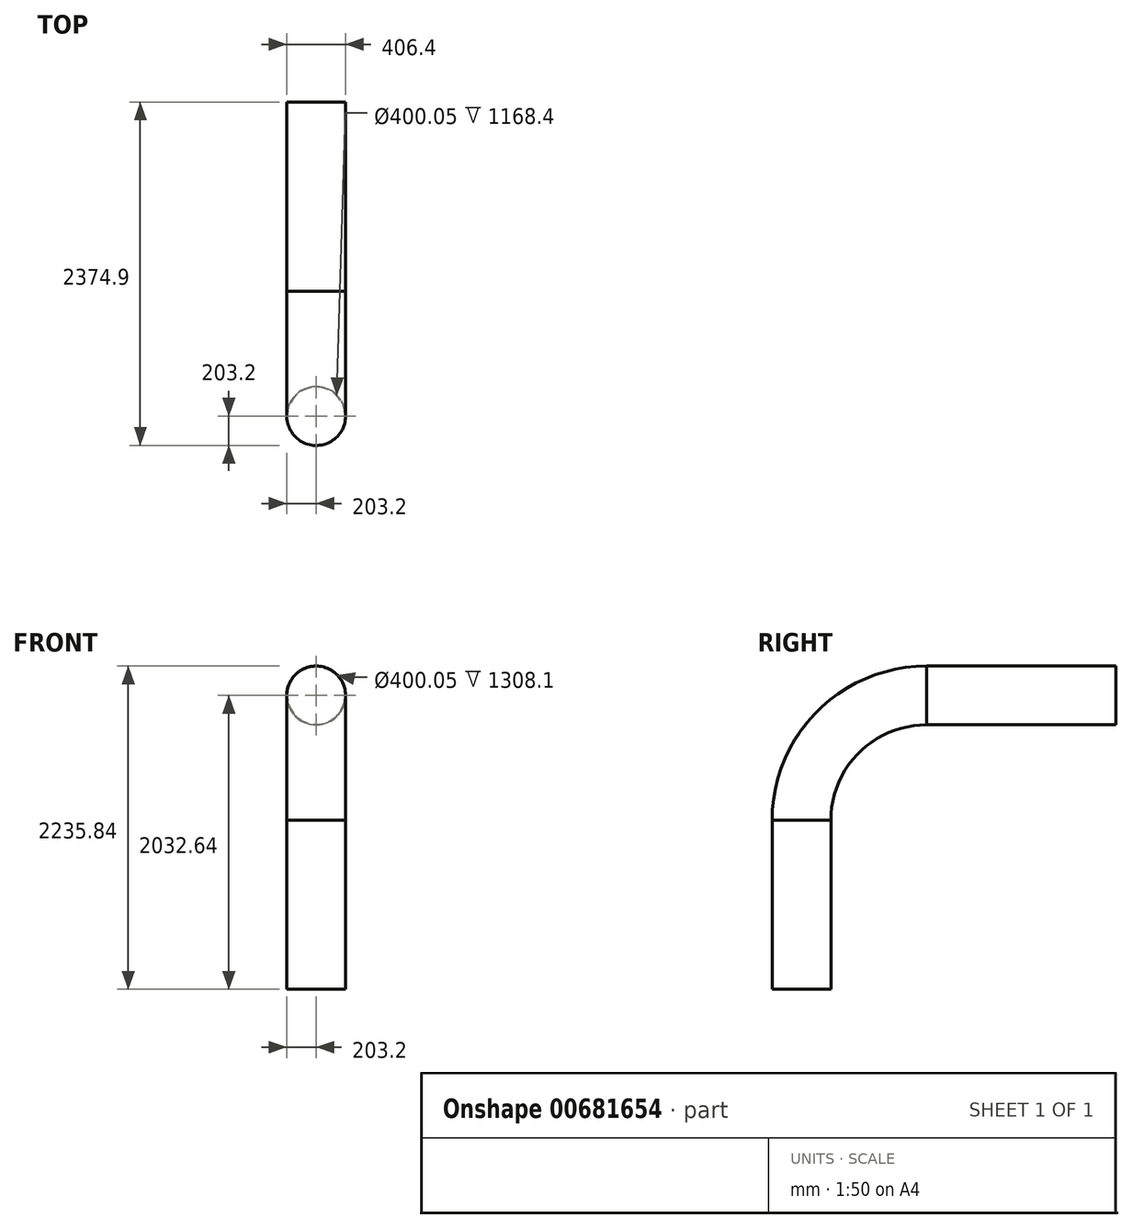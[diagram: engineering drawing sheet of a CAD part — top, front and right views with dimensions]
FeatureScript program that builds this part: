
annotation { "Feature Type Name" : "Feature", "Feature Type Description" : "" }
export const myFeature = defineFeature(function(context is Context, id is Id, definition is map)
    precondition{}
    {
        {
            var Q0;
            Q0=qCreatedBy(makeId("Right.planeOp"),FACE);
            var sketch = newSketch(context, id + "F0", { "sketchPlane" : qUnion([Q0])});
            skLineSegment(sketch, "E0", {"start": v(0, 0) * mm, "end": v(0, 1168.4) * mm, "construction": true});
            skLineSegment(sketch, "E1", {"start": v(0, 1168.4) * mm, "end": v(863.6, 1168.4) * mm, "construction": true});
            skLineSegment(sketch, "E2", {"start": v(863.6, 1168.4) * mm, "end": v(863.6, 2032) * mm, "construction": true});
            skLineSegment(sketch, "E3", {"start": v(863.6, 2032) * mm, "end": v(0, 2032) * mm, "construction": true});
            skLineSegment(sketch, "E4", {"start": v(0, 2032) * mm, "end": v(0, 1168.4) * mm, "construction": true});
            skSolve(sketch);
        }
        {
            var Q0;
            Q0=sQuery(id+"F0.wireOp",EDGE,"E1");
            cPlane(context, id + "F1", {"entities" : qUnion([Q0]), "cplaneType" : CPlaneType.LINE_ANGLE, "offset" : 25.4 * mm, "angle" : 0 * degree, "width" : 152.4 * mm, "height" : 152.4 * mm});
        }
        {
            var Q0;
            Q0=sQuery(id+"F0.wireOp",EDGE,"E2");
            cPlane(context, id + "F2", {"entities" : qUnion([Q0]), "cplaneType" : CPlaneType.LINE_ANGLE, "offset" : 25.4 * mm, "angle" : 90 * degree, "width" : 152.4 * mm, "height" : 152.4 * mm});
        }
        {
            var Q0;
            Q0=qCreatedBy(id+"F2.planeOp",FACE);
            var sketch = newSketch(context, id + "F3", { "sketchPlane" : qUnion([Q0])});
            skLineSegment(sketch, "E5", {"start": v(0, 1168.4) * mm, "end": v(203.2, 1168.4) * mm, "construction": true});
            skSolve(sketch);
        }
        {
            var Q0;
            Q0=qCreatedBy(makeId("Top.planeOp"),FACE);
            var sketch = newSketch(context, id + "F4", { "sketchPlane" : qUnion([Q0])});
            skCircle(sketch, "E6", {"center": v(0, 0) * mm, "radius": 203.2 * mm});
            skCircle(sketch, "E7", {"center": v(0, 0) * mm, "radius": 200.03 * mm});
            skSolve(sketch);
        }
        {
            var Q0;
            Q0=makeQuery(id+"F4.imprint","IMPRINT",FACE,{"disambiguationData":[TD([[makeQuery(id+"F4.imprint","IMPRINT",EDGE,{"derivedFrom":sQuery(id+"F4.wireOp",EDGE,"E6")}),1.0]])]});
            extrude(context, id + "F5", {"entities" : qUnion([Q0]), "depth" : 1168.4 * mm, "offsetDistance" : 25.4 * mm});
        }
        {
            var Q0;
            Q0=qCreatedBy(id+"F1.planeOp",FACE);
            var sketch = newSketch(context, id + "F6", { "sketchPlane" : qUnion([Q0])});
            skCircle(sketch, "E8", {"center": v(0, 0) * mm, "radius": 203.2 * mm});
            skCircle(sketch, "E9", {"center": v(0, 0) * mm, "radius": 200.03 * mm});
            skSolve(sketch);
        }
        {
            var Q0;
            Q0=makeQuery(id+"F6.imprint","IMPRINT",FACE,{"disambiguationData":[TD([[makeQuery(id+"F6.imprint","IMPRINT",EDGE,{"derivedFrom":sQuery(id+"F6.wireOp",EDGE,"E8")}),1.0]])]});
            var Q1;
            Q1=sQuery(id+"F3.wireOp",EDGE,"E5");
            revolve(context, id + "F7", {"surfaceOperationType" : NewSurfaceOperationType.NEW, "entities" : qUnion([Q0]), "axis" : qUnion([Q1]), "revolveType" : RevolveType.ONE_DIRECTION, "angle" : 90 * degree});
        }
        {
            var Q0;
            Q0=sQuery(id+"F0.wireOp",EDGE,"E3");
            cPlane(context, id + "F8", {"entities" : qUnion([Q0]), "cplaneType" : CPlaneType.LINE_ANGLE, "offset" : 25.4 * mm, "angle" : 90 * degree, "width" : 152.4 * mm, "height" : 152.4 * mm});
        }
        {
            var Q0;
            Q0=qCreatedBy(id+"F2.planeOp",FACE);
            var sketch = newSketch(context, id + "F9", { "sketchPlane" : qUnion([Q0])});
            skCircle(sketch, "E10", {"center": v(0, 2032.64) * mm, "radius": 203.2 * mm});
            skCircle(sketch, "E11", {"center": v(0, 2032.64) * mm, "radius": 200.03 * mm});
            skSolve(sketch);
        }
        {
            var Q0;
            Q0=makeQuery(id+"F9.imprint","IMPRINT",FACE,{"disambiguationData":[TD([[makeQuery(id+"F9.imprint","IMPRINT",EDGE,{"derivedFrom":sQuery(id+"F9.wireOp",EDGE,"E10")}),1.0]])]});
            extrude(context, id + "F10", {"entities" : qUnion([Q0]), "depth" : 1308.1 * mm, "offsetDistance" : 25.4 * mm});
        }
    });
